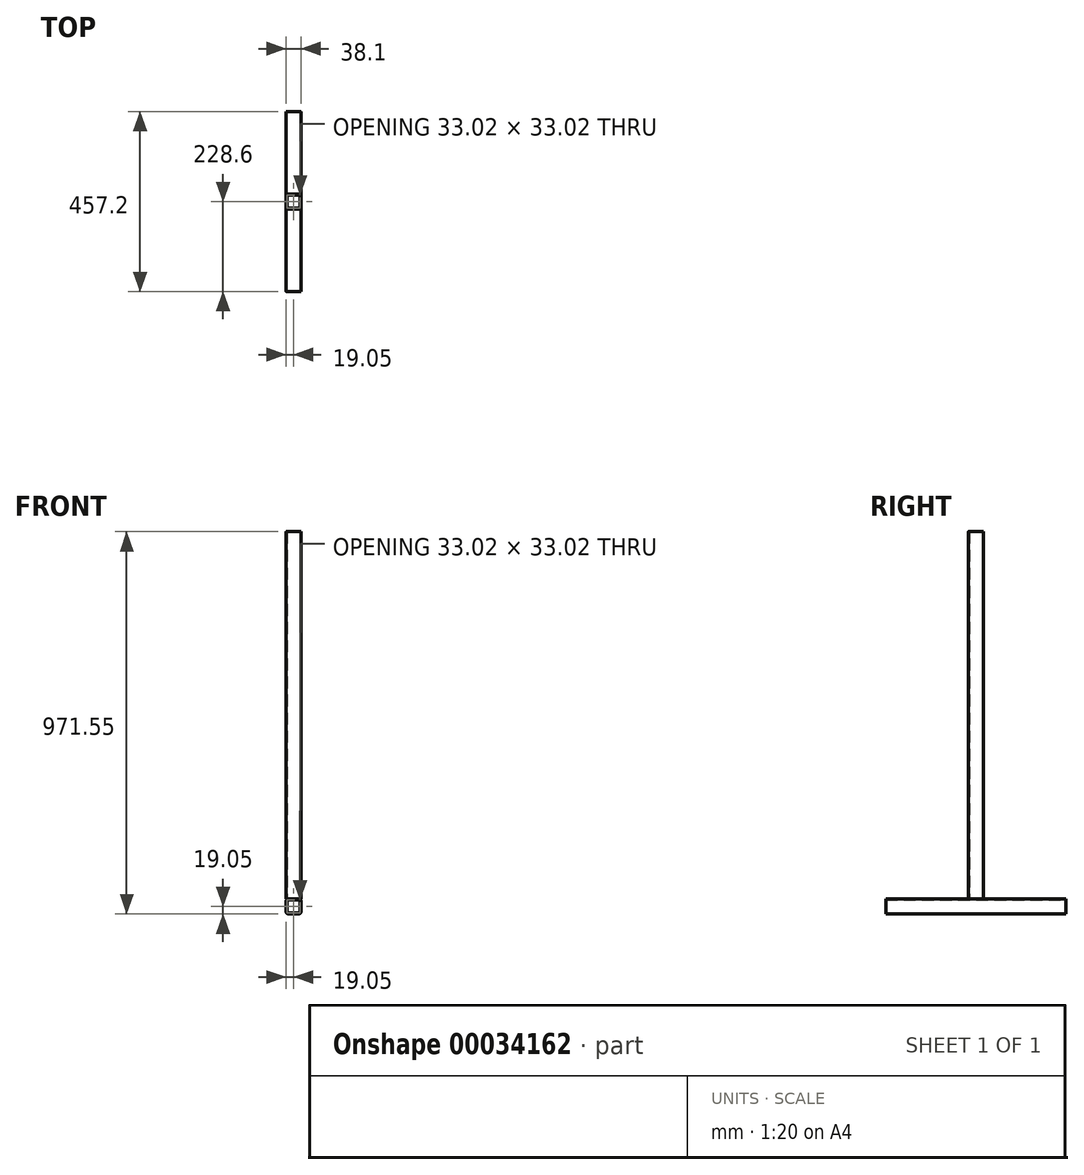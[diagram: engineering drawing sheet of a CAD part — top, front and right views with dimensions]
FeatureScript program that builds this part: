
annotation { "Feature Type Name" : "Feature", "Feature Type Description" : "" }
export const myFeature = defineFeature(function(context is Context, id is Id, definition is map)
    precondition{}
    {
        {
            var Q0;
            Q0=qCreatedBy(makeId("Top.planeOp"),FACE);
            var sketch = newSketch(context, id + "F0", { "sketchPlane" : qUnion([Q0])});
            skLineSegment(sketch, "E0.rect.bottom", {"start": v(12.7, 19.05) * mm, "end": v(-12.7, 19.05) * mm});
            skLineSegment(sketch, "E0.rect.top", {"start": v(12.7, -19.05) * mm, "end": v(-12.7, -19.05) * mm});
            skLineSegment(sketch, "E0.rect.left", {"start": v(19.05, 12.7) * mm, "end": v(19.05, -12.7) * mm});
            skLineSegment(sketch, "E0.rect.right", {"start": v(-19.05, 12.7) * mm, "end": v(-19.05, -12.7) * mm});
            skPoint(sketch, "E0.rect.middle", {"position": v(0, 0) * mm});
            skPoint(sketch, "E1.visualSharp", {"position": v(-19.05, 19.05) * mm});
            skArc(sketch, "E1.filletArc", {"start": v(-12.7, 19.05) * mm, "mid": v(-17.2, 17.2) * mm, "end": v(-19.05, 12.7) * mm});
            skPoint(sketch, "E2.visualSharp", {"position": v(19.05, 19.05) * mm});
            skArc(sketch, "E2.filletArc", {"start": v(19.05, 12.7) * mm, "mid": v(17.2, 17.2) * mm, "end": v(12.7, 19.05) * mm});
            skPoint(sketch, "E3.visualSharp", {"position": v(19.05, -19.05) * mm});
            skArc(sketch, "E3.filletArc", {"start": v(12.7, -19.05) * mm, "mid": v(17.2, -17.2) * mm, "end": v(19.05, -12.7) * mm});
            skPoint(sketch, "E4.visualSharp", {"position": v(-19.05, -19.05) * mm});
            skArc(sketch, "E4.filletArc", {"start": v(-19.05, -12.7) * mm, "mid": v(-17.2, -17.2) * mm, "end": v(-12.7, -19.05) * mm});
            skLineSegment(sketch, "E5.0", {"start": v(12.7, 16.51) * mm, "end": v(-12.7, 16.51) * mm});
            skArc(sketch, "E5.1", {"start": v(16.51, 12.7) * mm, "mid": v(15.4, 15.4) * mm, "end": v(12.7, 16.5) * mm});
            skLineSegment(sketch, "E5.2", {"start": v(16.51, 12.7) * mm, "end": v(16.51, -12.7) * mm});
            skArc(sketch, "E5.3", {"start": v(12.7, -16.5) * mm, "mid": v(15.4, -15.4) * mm, "end": v(16.51, -12.7) * mm});
            skLineSegment(sketch, "E5.4", {"start": v(12.7, -16.5) * mm, "end": v(-12.7, -16.5) * mm});
            skArc(sketch, "E5.5", {"start": v(-12.7, 16.51) * mm, "mid": v(-15.4, 15.4) * mm, "end": v(-16.51, 12.7) * mm});
            skArc(sketch, "E5.6", {"start": v(-16.51, -12.7) * mm, "mid": v(-15.4, -15.4) * mm, "end": v(-12.7, -16.5) * mm});
            skLineSegment(sketch, "E5.7", {"start": v(-16.51, 12.7) * mm, "end": v(-16.51, -12.7) * mm});
            skSolve(sketch);
        }
        {
            var Q0;
            Q0=qSketchRegion(id+"F0",true);
            extrude(context, id + "F1", {"entities" : qUnion([Q0]), "depth" : 19.05 * mm, "hasSecondDirection" : true, "secondDirectionOppositeDirection" : true, "secondDirectionDepth" : 914.4 * mm});
        }
        {
            var Q0;
            Q0=qCreatedBy(makeId("Front.planeOp"),FACE);
            var sketch = newSketch(context, id + "F2", { "sketchPlane" : qUnion([Q0])});
            skLineSegment(sketch, "E6.bottom", {"start": v(12.7, -952.5) * mm, "end": v(-12.7, -952.5) * mm});
            skLineSegment(sketch, "E6.top", {"start": v(12.7, -914.4) * mm, "end": v(-12.7, -914.4) * mm});
            skLineSegment(sketch, "E6.left", {"start": v(19.05, -946.15) * mm, "end": v(19.05, -920.75) * mm});
            skLineSegment(sketch, "E6.right", {"start": v(-19.05, -946.15) * mm, "end": v(-19.05, -920.75) * mm});
            skPoint(sketch, "E7.visualSharp", {"position": v(19.05, -914.4) * mm});
            skArc(sketch, "E7.filletArc", {"start": v(19.05, -920.75) * mm, "mid": v(17.2, -916.26) * mm, "end": v(12.7, -914.4) * mm});
            skPoint(sketch, "E8.visualSharp", {"position": v(19.05, -952.5) * mm});
            skArc(sketch, "E8.filletArc", {"start": v(12.7, -952.5) * mm, "mid": v(17.2, -950.64) * mm, "end": v(19.05, -946.15) * mm});
            skPoint(sketch, "E9.visualSharp", {"position": v(-19.05, -952.5) * mm});
            skArc(sketch, "E9.filletArc", {"start": v(-19.05, -946.15) * mm, "mid": v(-17.2, -950.64) * mm, "end": v(-12.7, -952.5) * mm});
            skPoint(sketch, "E10.visualSharp", {"position": v(-19.05, -914.4) * mm});
            skArc(sketch, "E10.filletArc", {"start": v(-12.7, -914.4) * mm, "mid": v(-17.2, -916.26) * mm, "end": v(-19.05, -920.75) * mm});
            skArc(sketch, "E11.0", {"start": v(16.51, -920.75) * mm, "mid": v(15.4, -918.06) * mm, "end": v(12.7, -916.94) * mm});
            skLineSegment(sketch, "E11.1", {"start": v(16.51, -946.15) * mm, "end": v(16.51, -920.75) * mm});
            skArc(sketch, "E11.2", {"start": v(12.7, -949.96) * mm, "mid": v(15.4, -948.84) * mm, "end": v(16.51, -946.15) * mm});
            skLineSegment(sketch, "E11.3", {"start": v(12.7, -949.96) * mm, "end": v(-12.7, -949.96) * mm});
            skArc(sketch, "E11.4", {"start": v(-16.51, -946.15) * mm, "mid": v(-15.4, -948.84) * mm, "end": v(-12.7, -949.96) * mm});
            skLineSegment(sketch, "E11.5", {"start": v(12.7, -916.94) * mm, "end": v(-12.7, -916.94) * mm});
            skLineSegment(sketch, "E11.6", {"start": v(-16.51, -946.15) * mm, "end": v(-16.51, -920.75) * mm});
            skArc(sketch, "E11.7", {"start": v(-12.7, -916.94) * mm, "mid": v(-15.4, -918.06) * mm, "end": v(-16.51, -920.75) * mm});
            skLineSegment(sketch, "E12.2", {"start": v(6.35, 12.7) * mm, "end": v(-6.35, 12.7) * mm});
            skSolve(sketch);
        }
        {
            var Q0;
            Q0=qSketchRegion(id+"F2",true);
            extrude(context, id + "F3", {"entities" : qUnion([Q0]), "endBound" : BoundingType.SYMMETRIC, "depth" : 457.2 * mm});
        }
    });
